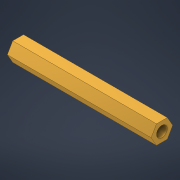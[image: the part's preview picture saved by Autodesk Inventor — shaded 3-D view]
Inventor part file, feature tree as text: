
AUTODESK INVENTOR PART (.ipt)
format: ipt  version: 2022 (Build 260153000, 153)  size: 97,280 bytes
history: native  units: mm
features: extrude x1, sketch x1
ambient origin geometry x8: Origin, YZ Plane, XZ Plane, XY Plane, X Axis, Y Axis, Z Axis, Center Point
bodies: Solid1 (feature_tree)
feature tree (2):
  extrude  "Extrusion1"  Depth=3.0mm
  sketch  "Sketch1"  dims[d0=6.0mm d1=3.0mm d2=40.0mm d3=0.0mm d4=5.196152mm]
